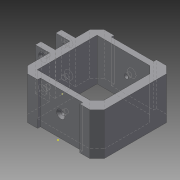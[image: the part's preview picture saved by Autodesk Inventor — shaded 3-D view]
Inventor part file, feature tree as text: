
AUTODESK INVENTOR PART (.ipt)
format: ipt  version: 2015 (Build 190159000, 159)  size: 172,544 bytes
history: native  units: mm
features: sketch x10, hole x5, extrude x3, chamfer x2
ambient origin geometry x8: Origin, YZ Plane, XZ Plane, XY Plane, X Axis, Y Axis, Z Axis, Center Point
bodies: Solid1 (feature_tree)
feature tree (20):
  extrude  "Extrusion1"  Depth=42.5mm
  chamfer  "Chamfer1"  Distance=30.0mm
  chamfer  "Chamfer2"  Distance=2.0mm Angle=45.0deg
  hole  "Hole1"  [1 undecoded]
  extrude  "Extrusion2"  Depth=30.0mm
  sketch  "Sketch4"  dims[d4=6.0mm]
  extrude  "Extrusion3"  Depth=2.0mm
  sketch  "Sketch6"  dims[d11=5.0mm d12=2.0mm d13=45.0deg d14=15.0mm]
  hole  "Hole2"  [1 undecoded]
  hole  "Hole3"  [1 undecoded]
  hole  "Hole4"  [1 undecoded]
  hole  "Hole5"  [1 undecoded]
  sketch  "Sketch1"  dims[d0=42.5mm d1=42.5mm]
  sketch  "Sketch2"  dims[d2=6.0mm]
  sketch  "Sketch3"  dims[d3=6.0mm]
  sketch  "Sketch5"  dims[d5=6.0mm d6=30.0mm d7=0.0mm d8=5.0mm d9=2.0mm d10=45.0deg]
  sketch  "Sketch7"  dims[d15=3.0mm d16=6.0mm d17=4.0mm d18=2.0mm d19=90.0deg d20=100.0mm d21=20.594885mm d22=30.0mm]
  sketch  "Sketch8"  dims[d23=6.25mm d24=2.0mm]
  sketch  "Sketch9"  dims[d25=2.0mm d26=30.0mm d27=0.0mm]
  sketch  "Sketch10"  dims[d28=10.5mm d29=4.0mm d30=4.0mm d31=5.25mm d32=10.0mm d33=0.0mm d34=3.0mm d35=6.0mm d36=6.0mm d37=2.0mm d38=90.0deg d39=100.0mm d40=20.594885mm d41=3.0mm d42=6.0mm d43=6.0mm d44=2.0mm d45=90.0deg d46=5.0mm d47=20.594885mm d48=5.0mm d49=5.0mm d50=3.0mm d51=6.0mm d52=6.0mm d53=2.0mm d54=90.0deg d55=5.0mm d56=20.594885mm d57=3.0mm d58=6.0mm d59=6.0mm d60=2.0mm d61=90.0deg d62=5.0mm d63=20.594885mm]
note: 5 required parameter values undecoded (feature->parameter linkage not recoverable at this tier; creation-order binding heuristic only, values carry confidence <= 0.55)
